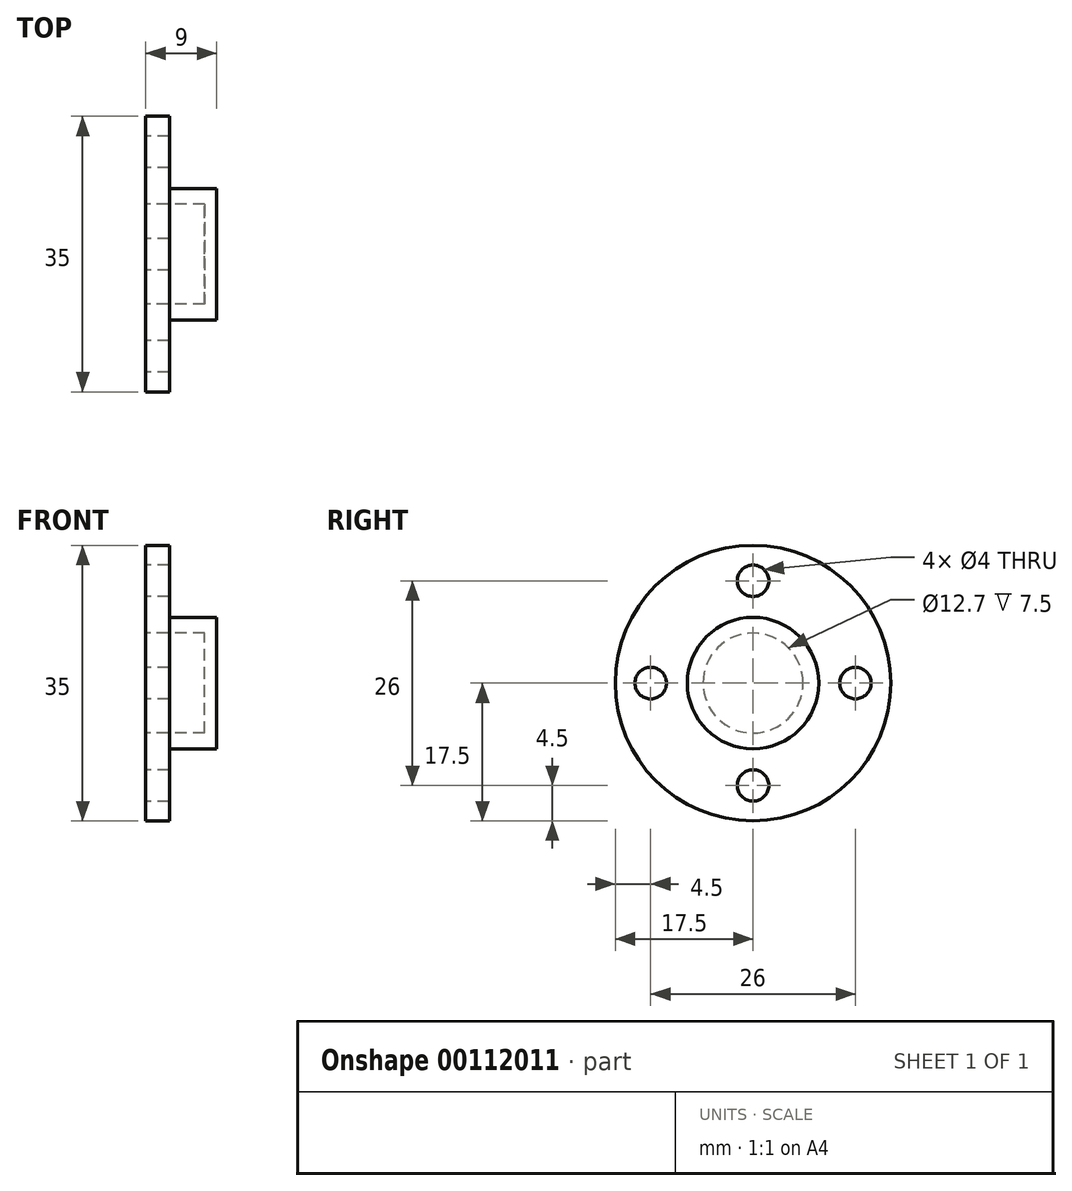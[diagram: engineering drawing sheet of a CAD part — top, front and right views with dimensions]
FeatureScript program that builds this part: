
annotation { "Feature Type Name" : "Feature", "Feature Type Description" : "" }
export const myFeature = defineFeature(function(context is Context, id is Id, definition is map)
    precondition{}
    {
        {
            var Q0;
            Q0=qCreatedBy(makeId("Right.planeOp"),FACE);
            var sketch = newSketch(context, id + "F0", { "sketchPlane" : qUnion([Q0])});
            skCircle(sketch, "E0", {"center": v(0, 0) * mm, "radius": 6.35 * mm});
            skCircle(sketch, "E1", {"center": v(0, 0) * mm, "radius": 13 * mm, "construction": true});
            skCircle(sketch, "E2", {"center": v(0, 0) * mm, "radius": 17.5 * mm});
            skCircle(sketch, "E3", {"center": v(0, 13) * mm, "radius": 2 * mm});
            skCircle(sketch, "E4", {"center": v(13, 0) * mm, "radius": 2 * mm});
            skCircle(sketch, "E5", {"center": v(0, -13) * mm, "radius": 2 * mm});
            skCircle(sketch, "E6", {"center": v(-13, 0) * mm, "radius": 2 * mm});
            skCircle(sketch, "E7", {"center": v(0, 13) * mm, "radius": 3.75 * mm, "construction": true});
            skSolve(sketch);
        }
        {
            var Q0;
            Q0 = qSketchRegion(id + "F0", true);
            extrude(context, id + "F1", {"entities" : qUnion([Q0]), "depth" : 9 * mm});
        }
        {
            var Q0;
            Q0=makeQuery(id+"F1.opExtrude","CAP_FACE",FACE,{"disambiguationData":[OSD([sQuery(id+"F0.wireOp",EDGE,"E0"),sQuery(id+"F0.wireOp",EDGE,"E2"),sQuery(id+"F0.wireOp",EDGE,"E3"),sQuery(id+"F0.wireOp",EDGE,"E4"),sQuery(id+"F0.wireOp",EDGE,"E5"),sQuery(id+"F0.wireOp",EDGE,"E6")])],"isStart":false});
            var sketch = newSketch(context, id + "F2", { "sketchPlane" : qUnion([Q0])});
            skCircle(sketch, "E8", {"center": v(0, 0) * mm, "radius": 8.35 * mm});
            skCircle(sketch, "E9", {"center": v(0, 0) * mm, "radius": 17.5 * mm});
            skCircle(sketch, "E10", {"center": v(0, 13) * mm, "radius": 3.75 * mm, "construction": true});
            skSolve(sketch);
        }
        {
            var Q0;
            Q0 = qSketchRegion(id + "F2", true);
            extrude(context, id + "F3", {"entities" : qUnion([Q0]), "operationType" : NewBodyOperationType.REMOVE, "oppositeDirection" : true, "depth" : 6 * mm});
        }
        {
            var Q0;
            Q0=makeQuery(id+"F1.opExtrude","CAP_FACE",FACE,{"disambiguationData":[OSD([sQuery(id+"F0.wireOp",EDGE,"E0"),sQuery(id+"F0.wireOp",EDGE,"E2"),sQuery(id+"F0.wireOp",EDGE,"E3"),sQuery(id+"F0.wireOp",EDGE,"E4"),sQuery(id+"F0.wireOp",EDGE,"E5"),sQuery(id+"F0.wireOp",EDGE,"E6")])],"isStart":false});
            var sketch = newSketch(context, id + "F4", { "sketchPlane" : qUnion([Q0])});
            skCircle(sketch, "E11", {"center": v(0, 0) * mm, "radius": 6.4 * mm});
            skSolve(sketch);
        }
        {
            var Q0;
            Q0 = qSketchRegion(id + "F4", true);
            extrude(context, id + "F5", {"entities" : qUnion([Q0]), "operationType" : NewBodyOperationType.ADD, "oppositeDirection" : true, "depth" : 1.5 * mm});
        }
    });
